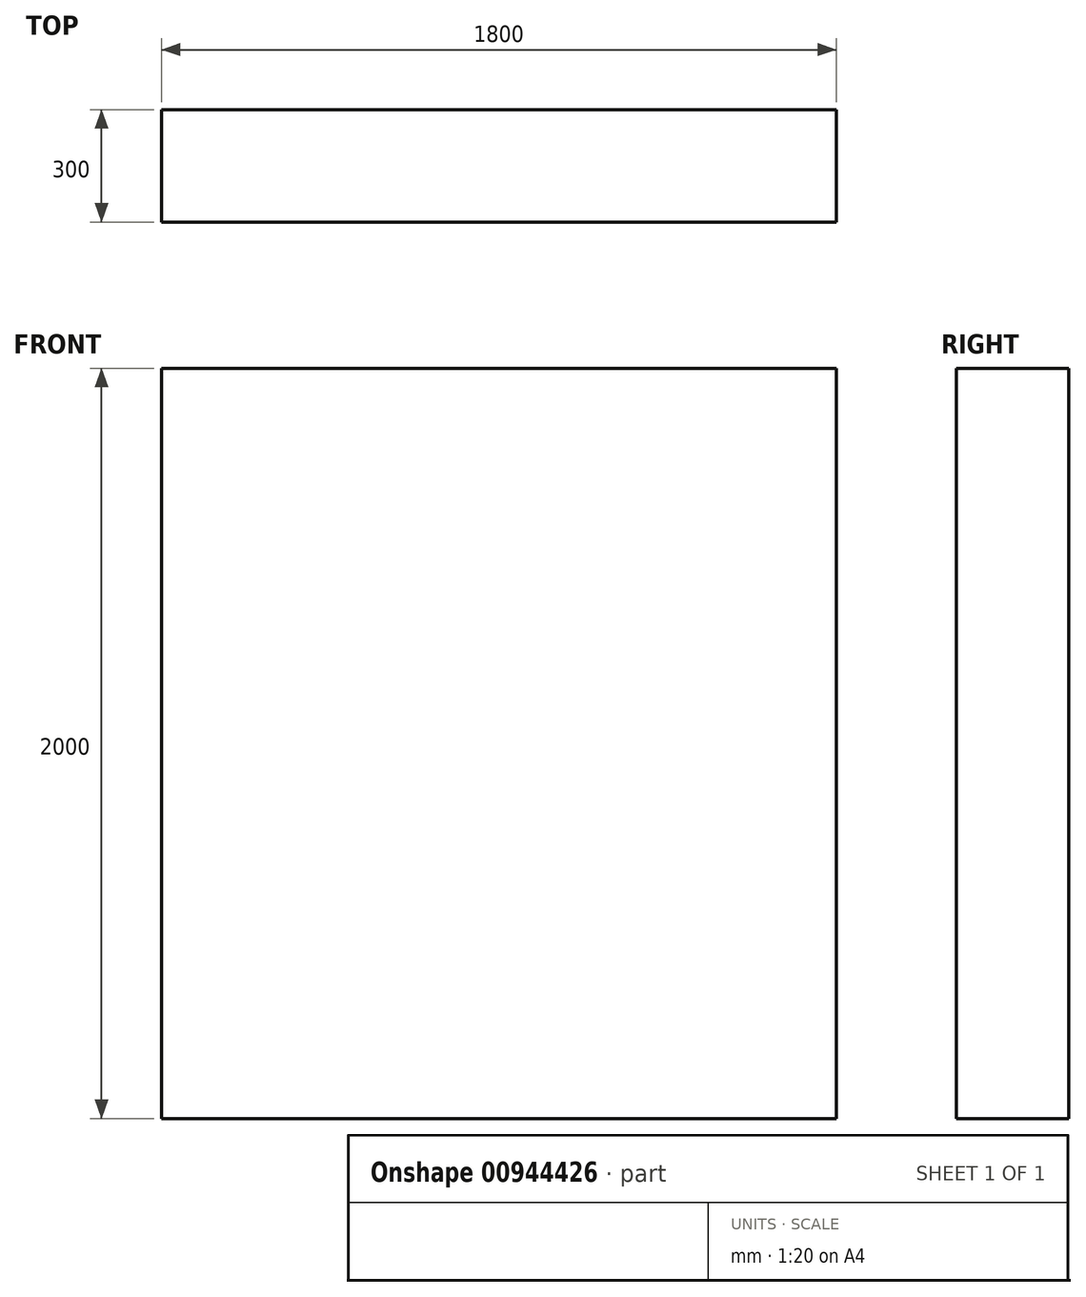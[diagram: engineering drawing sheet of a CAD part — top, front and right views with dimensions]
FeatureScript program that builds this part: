
annotation { "Feature Type Name" : "Feature", "Feature Type Description" : "" }
export const myFeature = defineFeature(function(context is Context, id is Id, definition is map)
    precondition{}
    {
        {
            var Q0;
            Q0=qCreatedBy(makeId("Front.planeOp"),FACE);
            var sketch = newSketch(context, id + "F0", { "sketchPlane" : qUnion([Q0])});
            skLineSegment(sketch, "E0.bottom", {"start": v(900, 1000) * mm, "end": v(-900, 1000) * mm});
            skLineSegment(sketch, "E0.top", {"start": v(900, -1000) * mm, "end": v(-900, -1000) * mm});
            skLineSegment(sketch, "E0.left", {"start": v(900, 1000) * mm, "end": v(900, -1000) * mm});
            skLineSegment(sketch, "E0.right", {"start": v(-900, 1000) * mm, "end": v(-900, -1000) * mm});
            skPoint(sketch, "E0.middle", {"position": v(0, 0) * mm});
            skSolve(sketch);
        }
        {
            var Q0;
            Q0 = qSketchRegion(id + "F0", true);
            extrude(context, id + "F1", {"entities" : qUnion([Q0]), "depth" : 300 * mm, "offsetDistance" : 25 * mm});
        }
    });
